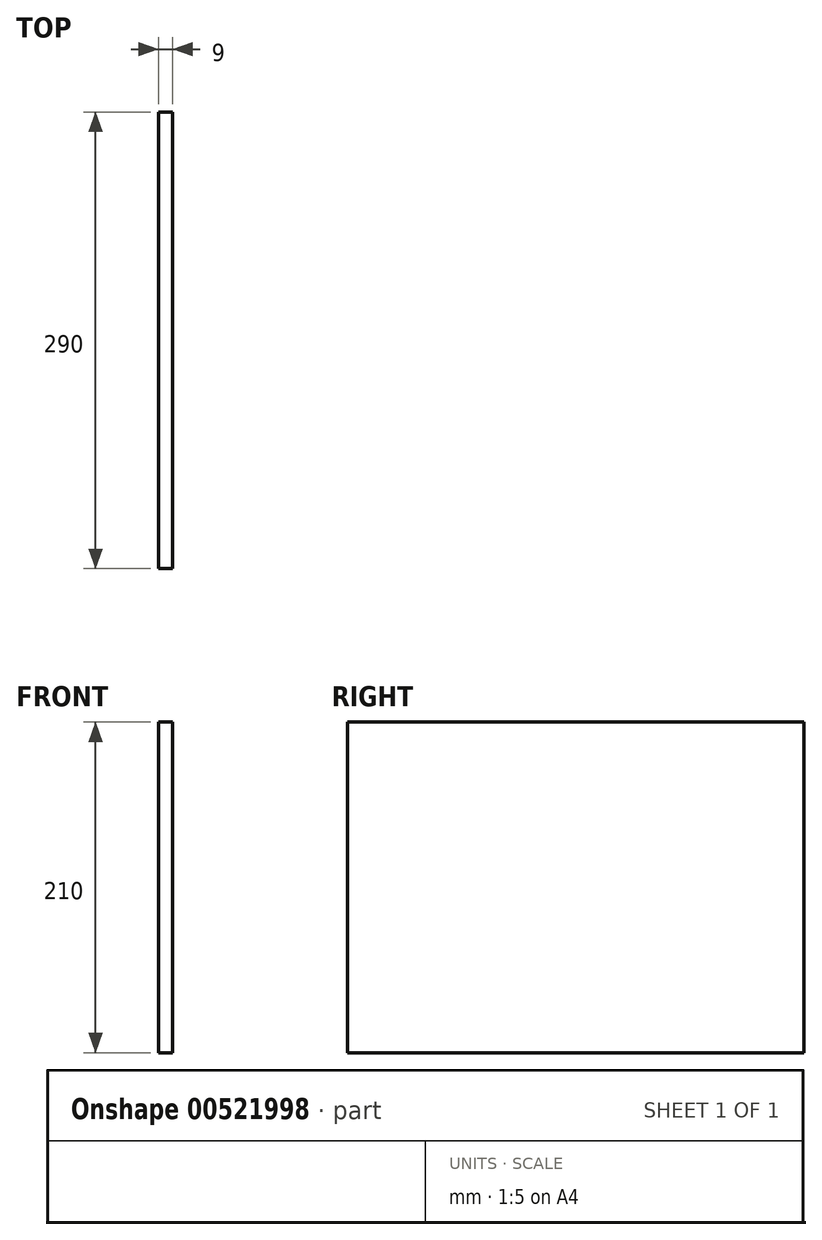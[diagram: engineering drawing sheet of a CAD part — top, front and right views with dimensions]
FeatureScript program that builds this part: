
annotation { "Feature Type Name" : "Feature", "Feature Type Description" : "" }
export const myFeature = defineFeature(function(context is Context, id is Id, definition is map)
    precondition{}
    {
        {
            var Q0;
            Q0=qCreatedBy(makeId("Right.planeOp"),FACE);
            var sketch = newSketch(context, id + "F0", { "sketchPlane" : qUnion([Q0])});
            skLineSegment(sketch, "E0.bottom", {"start": v(0, 0) * mm, "end": v(-290, 0) * mm});
            skLineSegment(sketch, "E0.top", {"start": v(0, 210) * mm, "end": v(-290, 210) * mm});
            skLineSegment(sketch, "E0.left", {"start": v(0, 0) * mm, "end": v(0, 210) * mm});
            skLineSegment(sketch, "E0.right", {"start": v(-290, 0) * mm, "end": v(-290, 210) * mm});
            skSolve(sketch);
        }
        {
            var Q0;
            Q0=makeQuery(id+"F0.imprint","IMPRINT",FACE,{"disambiguationData":[TD([[makeQuery(id+"F0.imprint","IMPRINT",EDGE,{"derivedFrom":sQuery(id+"F0.wireOp",EDGE,"E0.bottom")}),-1.0]])]});
            extrude(context, id + "F1", {"entities" : qUnion([Q0]), "depth" : 9 * mm, "offsetDistance" : 25 * mm});
        }
    });
